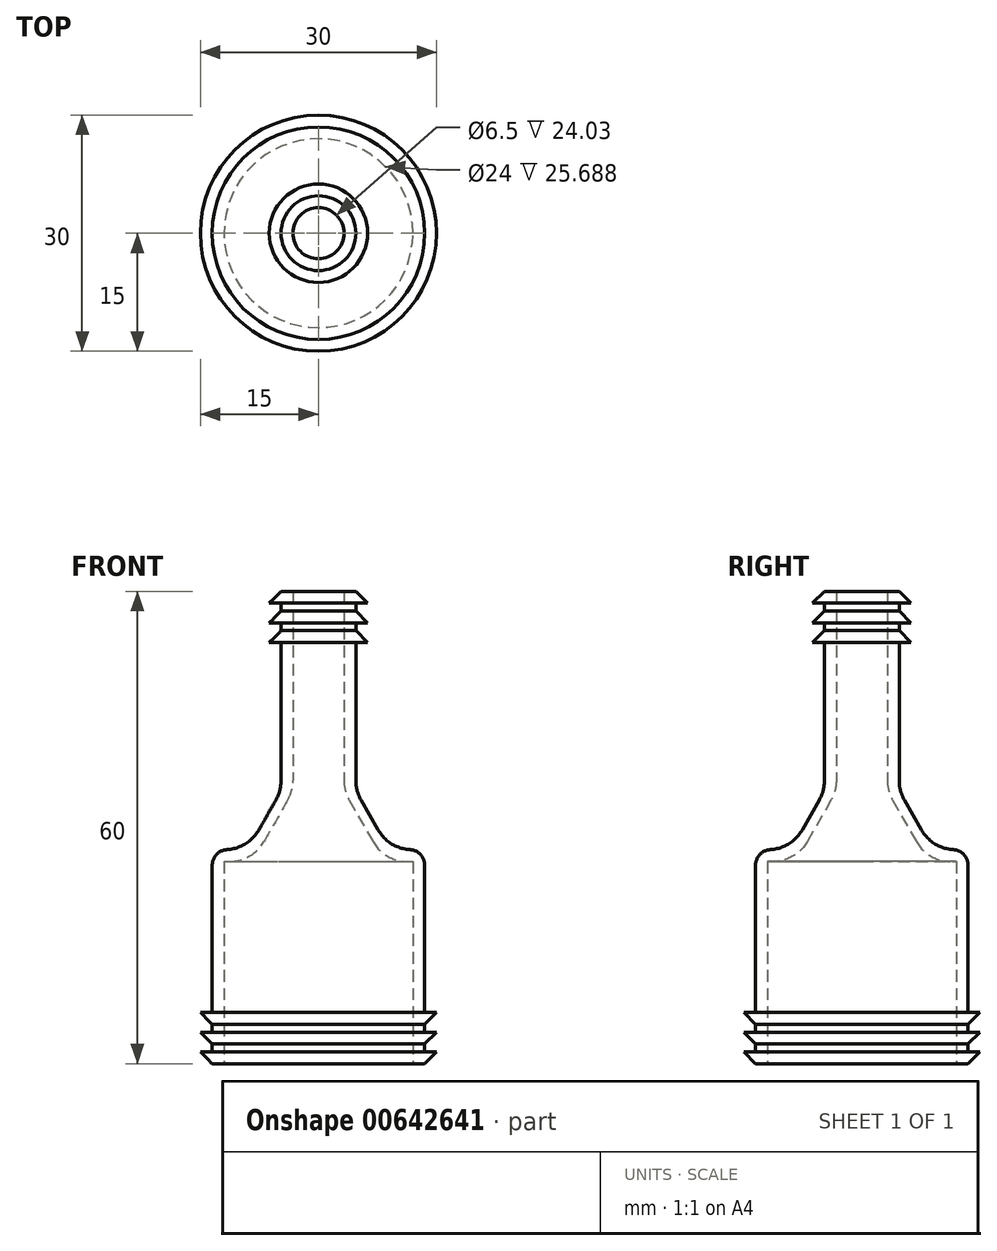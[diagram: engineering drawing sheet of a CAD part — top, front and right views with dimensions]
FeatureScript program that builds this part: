
annotation { "Feature Type Name" : "Feature", "Feature Type Description" : "" }
export const myFeature = defineFeature(function(context is Context, id is Id, definition is map)
    precondition{}
    {
        {
            var Q0;
            Q0=qCreatedBy(makeId("Front.planeOp"),FACE);
            var sketch = newSketch(context, id + "F0", { "sketchPlane" : qUnion([Q0])});
            skLineSegment(sketch, "E0", {"start": v(0, 0) * mm, "end": v(0, 86.11) * mm, "construction": true});
            skLineSegment(sketch, "E1", {"start": v(-13.5, 1.5) * mm, "end": v(-13.5, 2.5) * mm});
            skLineSegment(sketch, "E2", {"start": v(-13.5, 27.19) * mm, "end": v(-11.9, 27.19) * mm});
            skLineSegment(sketch, "E3", {"start": v(-4.75, 35.97) * mm, "end": v(-4.75, 53.5) * mm});
            skLineSegment(sketch, "E4.0", {"start": v(-3.25, 35.97) * mm, "end": v(-3.25, 60) * mm});
            skLineSegment(sketch, "E4.1", {"start": v(-12, 25.69) * mm, "end": v(-11.26, 25.69) * mm});
            skLineSegment(sketch, "E4.2", {"start": v(-12, 0) * mm, "end": v(-12, 25.69) * mm});
            skLineSegment(sketch, "E5", {"start": v(-13.5, 0) * mm, "end": v(-12, 0) * mm});
            skLineSegment(sketch, "E6", {"start": v(-4.75, 60) * mm, "end": v(-3.25, 60) * mm});
            skLineSegment(sketch, "E7", {"start": v(-15, 0) * mm, "end": v(-15, 63.37) * mm, "construction": true});
            skLineSegment(sketch, "E8", {"start": v(-13.5, 0) * mm, "end": v(-15, 1.5) * mm});
            skLineSegment(sketch, "E9", {"start": v(-15, 1.5) * mm, "end": v(-13.5, 1.5) * mm});
            skLineSegment(sketch, "E10", {"start": v(-13.5, 2.5) * mm, "end": v(-15, 4) * mm});
            skLineSegment(sketch, "E11", {"start": v(-15, 4) * mm, "end": v(-13.5, 4) * mm});
            skLineSegment(sketch, "E12", {"start": v(-13.5, 5) * mm, "end": v(-15, 6.5) * mm});
            skLineSegment(sketch, "E13", {"start": v(-15, 6.5) * mm, "end": v(-13.5, 6.5) * mm});
            skLineSegment(sketch, "E14.trimOffspring", {"start": v(-13.5, 6.5) * mm, "end": v(-13.5, 27.19) * mm});
            skLineSegment(sketch, "E15.trimOffspring", {"start": v(-13.5, 4) * mm, "end": v(-13.5, 5) * mm});
            skLineSegment(sketch, "E16", {"start": v(-6.25, 66.68) * mm, "end": v(-6.25, 31.16) * mm, "construction": true});
            skLineSegment(sketch, "E17", {"start": v(-4.75, 60) * mm, "end": v(-6.25, 58.5) * mm});
            skLineSegment(sketch, "E18", {"start": v(-6.25, 58.5) * mm, "end": v(-4.75, 58.5) * mm});
            skLineSegment(sketch, "E19", {"start": v(-4.75, 57.5) * mm, "end": v(-6.25, 56) * mm});
            skLineSegment(sketch, "E20", {"start": v(-6.25, 56) * mm, "end": v(-4.75, 56) * mm});
            skLineSegment(sketch, "E21", {"start": v(-4.75, 55) * mm, "end": v(-6.25, 53.5) * mm});
            skLineSegment(sketch, "E22", {"start": v(-6.25, 53.5) * mm, "end": v(-4.75, 53.5) * mm});
            skLineSegment(sketch, "E23", {"start": v(-5.4, 33.5) * mm, "end": v(-7.56, 29.71) * mm});
            skLineSegment(sketch, "E24", {"start": v(-3.9, 33.5) * mm, "end": v(-6.92, 28.21) * mm});
            skLineSegment(sketch, "E25.trimOffspring", {"start": v(-4.75, 57.5) * mm, "end": v(-4.75, 58.5) * mm});
            skLineSegment(sketch, "E26.trimOffspring", {"start": v(-4.75, 55) * mm, "end": v(-4.75, 56) * mm});
            skPoint(sketch, "E27.visualSharp", {"position": v(-3.25, 34.64) * mm});
            skArc(sketch, "E27.filletArc", {"start": v(-3.9, 33.5) * mm, "mid": v(-3.42, 34.69) * mm, "end": v(-3.25, 35.97) * mm});
            skPoint(sketch, "E28.visualSharp", {"position": v(-4.75, 34.64) * mm});
            skArc(sketch, "E28.filletArc", {"start": v(-5.4, 33.5) * mm, "mid": v(-4.92, 34.69) * mm, "end": v(-4.75, 35.97) * mm});
            skPoint(sketch, "E29.visualSharp", {"position": v(-8.36, 25.69) * mm});
            skArc(sketch, "E29.filletArc", {"start": v(-11.26, 25.69) * mm, "mid": v(-8.75, 26.36) * mm, "end": v(-6.92, 28.21) * mm});
            skPoint(sketch, "E30.visualSharp", {"position": v(-9, 27.19) * mm});
            skArc(sketch, "E30.filletArc", {"start": v(-11.9, 27.19) * mm, "mid": v(-9.4, 27.86) * mm, "end": v(-7.56, 29.71) * mm});
            skSolve(sketch);
        }
        {
            var Q0;
            Q0 = qSketchRegion(id + "F0", true);
            var Q1;
            Q1=sQuery(id+"F0.wireOp",EDGE,"E0");
            revolve(context, id + "F1", {"entities" : qUnion([Q0]), "axis" : qUnion([Q1]), "revolveType" : RevolveType.FULL});
        }
        {
            var Q0;
            Q0=makeQuery(id+"F1.opRevolve","SWEPT_EDGE",EDGE,{"disambiguationData":[OSD([sQuery(id+"F0.wireOp",EDGE,"E2"),sQuery(id+"F0.wireOp",EDGE,"E14.trimOffspring")])]});
            fillet(context, id + "F2", {"entities" : qUnion([Q0]), "radius" : 2 * mm, "tangentPropagation" : true, "allowEdgeOverflow" : false});
        }
    });
